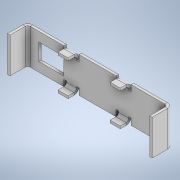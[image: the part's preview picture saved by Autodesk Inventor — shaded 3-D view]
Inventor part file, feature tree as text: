
AUTODESK INVENTOR PART (.ipt)
format: ipt  version: 2021 (Build 250183000, 183)  size: 214,528 bytes
history: native  units: mm
features: other x10, sketch x5, sheet_metal_op x3, mirror x2
ambient origin geometry x8: Origin, YZ Plane, XZ Plane, XY Plane, X Axis, Y Axis, Z Axis, Center Point
bodies: Body1 (feature_tree)
feature tree (20):
  other  "Sólido1"
  sheet_metal_op  "Face1"
  sheet_metal_op  "Flange1"
  sheet_metal_op  "Flange2"
  mirror  "Espelhamento1"
  mirror  "Espelhamento2"
  sketch  "Esboço1"  dims[d0=172.0mm]
  other  "Placa1"
  sketch  "Esboço2"  dims[d1=42.0mm]
  other  "Placa2"
  other  "Vergadura1"
  other  "Canto1"
  sketch  "Esboço3"  dims[d2=3.0mm]
  sketch  "Esboço4"  dims[d3=3.0mm]
  other  "Placa3"
  other  "Vergadura2"
  other  "Canto2"
  sketch  "Esboço5"  dims[d4=1.5mm d5=6.0mm d6=3.0mm d7=21.0mm d8=90.0deg d9=3.0mm d10=12.0mm d11=3.0mm d12=3.0mm d13=180.0deg d15=18.0mm d16=3.0mm d17=3.0mm d18=0.0mm d19=3.0mm d20=1.5mm d21=6.0mm d22=3.0mm d23=10.0mm d24=90.0deg d25=3.0mm d26=12.0mm d27=3.0mm d28=3.0mm d29=30.0mm d30=20.0mm d31=3.0mm d32=0.0mm]
  other  "Recortar1"
  other  "Recortar2"
